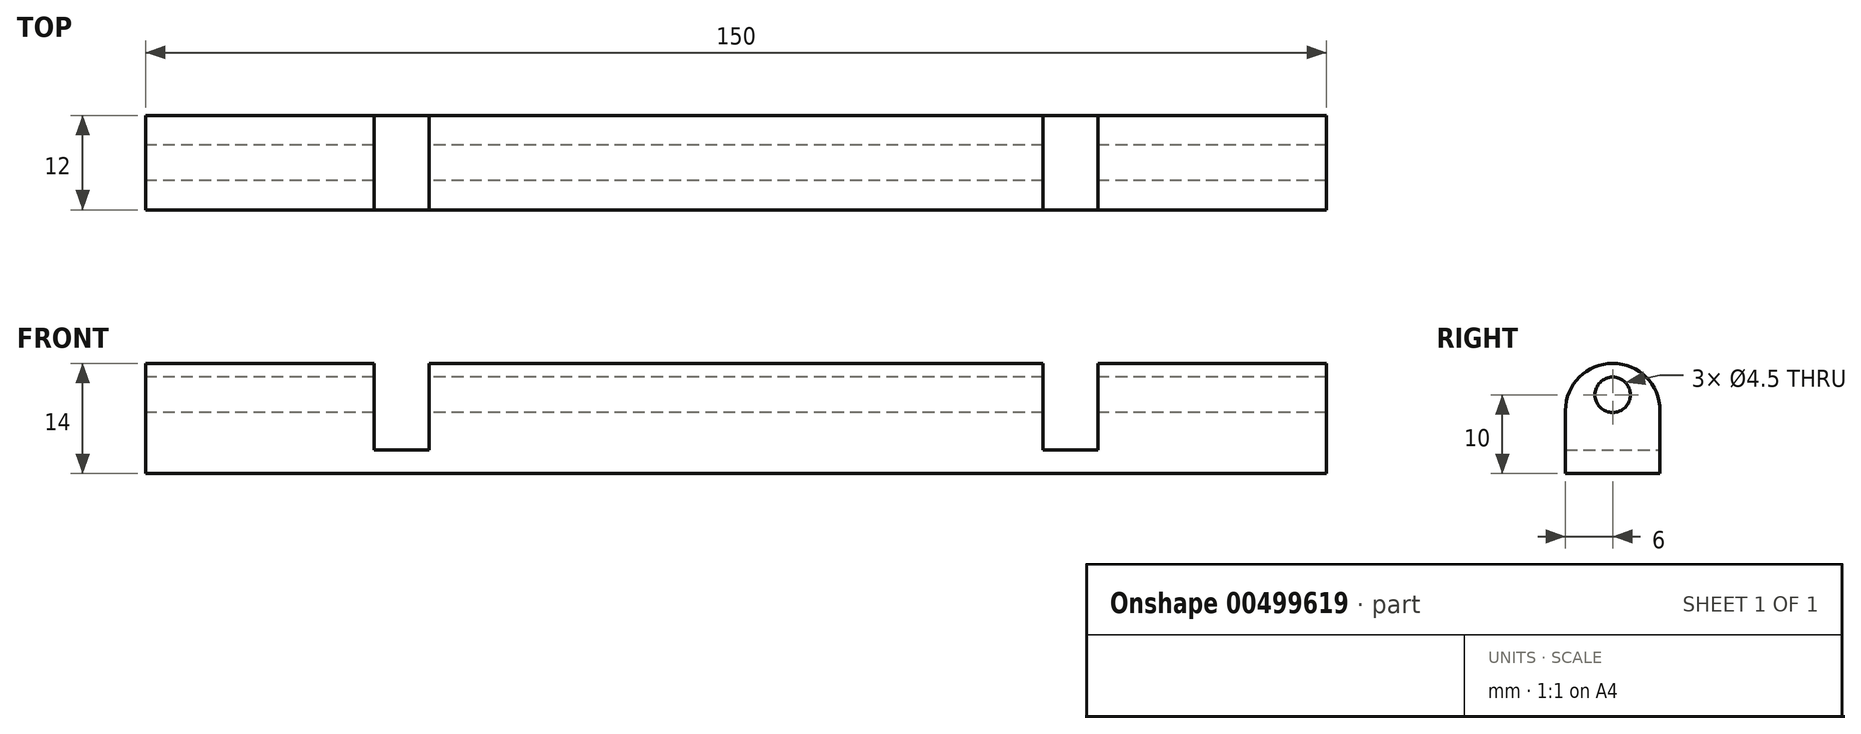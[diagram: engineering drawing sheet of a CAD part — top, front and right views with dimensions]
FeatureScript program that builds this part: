
annotation { "Feature Type Name" : "Feature", "Feature Type Description" : "" }
export const myFeature = defineFeature(function(context is Context, id is Id, definition is map)
    precondition{}
    {
        {
            var Q0;
            Q0=qCreatedBy(makeId("Top.planeOp"),FACE);
            var sketch = newSketch(context, id + "F0", { "sketchPlane" : qUnion([Q0])});
            skLineSegment(sketch, "E0.bottom", {"start": v(0, 0) * mm, "end": v(150, 0) * mm});
            skLineSegment(sketch, "E0.top", {"start": v(0, 12) * mm, "end": v(150, 12) * mm});
            skLineSegment(sketch, "E0.left", {"start": v(0, 0) * mm, "end": v(0, 12) * mm});
            skLineSegment(sketch, "E0.right", {"start": v(150, 0) * mm, "end": v(150, 12) * mm});
            skSolve(sketch);
        }
        {
            var Q0;
            Q0=makeQuery(id+"F0.imprint","IMPRINT",FACE,{"disambiguationData":[TD([[makeQuery(id+"F0.imprint","IMPRINT",EDGE,{"derivedFrom":sQuery(id+"F0.wireOp",EDGE,"E0.bottom")}),1.0]])]});
            extrude(context, id + "F1", {"entities" : qUnion([Q0]), "depth" : 3 * mm, "hasSecondDirection" : true, "secondDirectionOppositeDirection" : true, "secondDirectionDepth" : 0 * mm, "offsetDistance" : 25 * mm});
        }
        {
            var Q0;
            Q0=makeQuery(id+"F1.opExtrude","SWEPT_FACE",FACE,{"disambiguationData":[OSD([sQuery(id+"F0.wireOp",EDGE,"E0.left")])]});
            var sketch = newSketch(context, id + "F2", { "sketchPlane" : qUnion([Q0])});
            skLineSegment(sketch, "E1", {"start": v(-12, 3) * mm, "end": v(-12, 8) * mm});
            skLineSegment(sketch, "E2", {"start": v(0, 3) * mm, "end": v(0, 8) * mm});
            skArc(sketch, "E3", {"start": v(0, 8) * mm, "mid": v(-6, 14) * mm, "end": v(-12, 8) * mm});
            skCircle(sketch, "E4", {"center": v(-6, 10) * mm, "radius": 2.25 * mm});
            skSolve(sketch);
        }
        {
            var Q0;
            Q0=makeQuery(id+"F2.imprint","IMPRINT",FACE,{"disambiguationData":[TD([[makeQuery(id+"F2.imprint","IMPRINT",EDGE,{"derivedFrom":sQuery(id+"F2.wireOp",EDGE,"E1")}),-1.0]])]});
            extrude(context, id + "F3", {"entities" : qUnion([Q0]), "operationType" : NewBodyOperationType.ADD, "oppositeDirection" : true, "depth" : 29 * mm});
        }
        {
            var Q0;
            Q0=makeQuery(id+"F2.imprint","IMPRINT",FACE,{"disambiguationData":[TD([[makeQuery(id+"F2.imprint","IMPRINT",EDGE,{"derivedFrom":sQuery(id+"F2.wireOp",EDGE,"E1")}),-1.0]])]});
            extrude(context, id + "F4", {"entities" : qUnion([Q0]), "operationType" : NewBodyOperationType.ADD, "oppositeDirection" : true, "depth" : 114 * mm, "hasSecondDirection" : true, "secondDirectionOppositeDirection" : true, "secondDirectionDepth" : 36 * mm});
        }
        {
            var Q0;
            Q0=makeQuery(id+"F2.imprint","IMPRINT",FACE,{"disambiguationData":[TD([[makeQuery(id+"F2.imprint","IMPRINT",EDGE,{"derivedFrom":sQuery(id+"F2.wireOp",EDGE,"E1")}),-1.0]])]});
            extrude(context, id + "F5", {"entities" : qUnion([Q0]), "operationType" : NewBodyOperationType.ADD, "oppositeDirection" : true, "depth" : 150 * mm, "hasSecondDirection" : true, "secondDirectionOppositeDirection" : true, "secondDirectionDepth" : 121 * mm});
        }
    });
